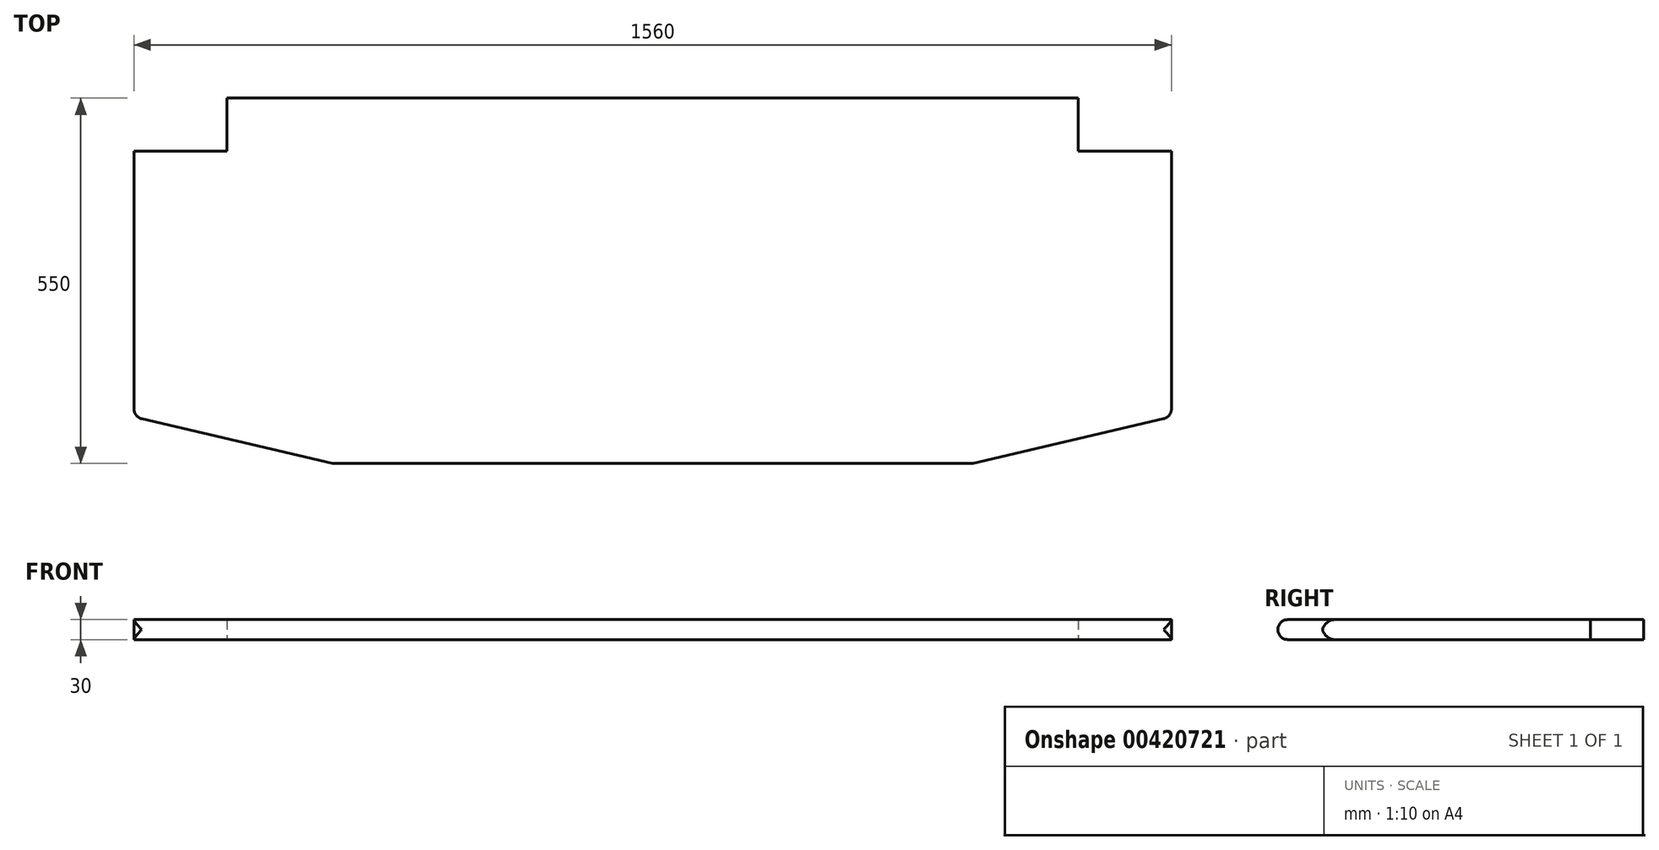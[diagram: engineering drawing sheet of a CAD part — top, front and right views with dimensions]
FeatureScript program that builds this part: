
annotation { "Feature Type Name" : "Feature", "Feature Type Description" : "" }
export const myFeature = defineFeature(function(context is Context, id is Id, definition is map)
    precondition{}
    {
        {
            var Q0;
            Q0=qCreatedBy(makeId("Top.planeOp"),FACE);
            cPlane(context, id + "F0", {"entities" : qUnion([Q0]), "cplaneType" : CPlaneType.OFFSET, "offset" : 750 * mm, "width" : 150 * mm, "height" : 150 * mm});
        }
        {
            var Q0;
            Q0=qCreatedBy(id+"F0.planeOp",FACE);
            var sketch = newSketch(context, id + "F1", { "sketchPlane" : qUnion([Q0])});
            skLineSegment(sketch, "E0", {"start": v(-640, 0) * mm, "end": v(640, 0) * mm});
            skLineSegment(sketch, "E1", {"start": v(780, -80) * mm, "end": v(780, -480) * mm});
            skLineSegment(sketch, "E2", {"start": v(780, -480) * mm, "end": v(480, -550) * mm});
            skLineSegment(sketch, "E3", {"start": v(480, -550) * mm, "end": v(-480, -550) * mm});
            skLineSegment(sketch, "E4", {"start": v(-480, -550) * mm, "end": v(-780, -480) * mm});
            skLineSegment(sketch, "E5", {"start": v(-780, -480) * mm, "end": v(-780, -80) * mm});
            skLineSegment(sketch, "E6", {"start": v(-780, -80) * mm, "end": v(-640, -80) * mm});
            skLineSegment(sketch, "E7", {"start": v(-640, -80) * mm, "end": v(-640, 0) * mm});
            skLineSegment(sketch, "E8", {"start": v(780, -80) * mm, "end": v(640, -80) * mm});
            skLineSegment(sketch, "E9", {"start": v(640, -80) * mm, "end": v(640, 0) * mm});
            skPoint(sketch, "E10.orphan", {"position": v(-780, 0) * mm});
            skPoint(sketch, "E11.orphan", {"position": v(780, 0) * mm});
            skSolve(sketch);
        }
        {
            var Q0;
            Q0 = qSketchRegion(id + "F1", true);
            extrude(context, id + "F2", {"entities" : qUnion([Q0]), "depth" : 30 * mm});
        }
        {
            var Q0;
            Q0=makeQuery(id+"F2.opExtrude","CAP_EDGE",EDGE,{"disambiguationData":[OSD([sQuery(id+"F1.wireOp",EDGE,"E4")])],"isStart":false});
            var Q1;
            Q1=makeQuery(id+"F2.opExtrude","SWEPT_FACE",FACE,{"disambiguationData":[OSD([sQuery(id+"F1.wireOp",EDGE,"E4")])]});
            var Q2;
            Q2=makeQuery(id+"F2.opExtrude","SWEPT_FACE",FACE,{"disambiguationData":[OSD([sQuery(id+"F1.wireOp",EDGE,"E3")])]});
            var Q3;
            Q3=makeQuery(id+"F2.opExtrude","SWEPT_FACE",FACE,{"disambiguationData":[OSD([sQuery(id+"F1.wireOp",EDGE,"E2")])]});
            var Q4;
            Q4=makeQuery(id+"F2.opExtrude","SWEPT_EDGE",EDGE,{"disambiguationData":[OSD([sQuery(id+"F1.wireOp",EDGE,"E3"),sQuery(id+"F1.wireOp",EDGE,"E4")])]});
            fillet(context, id + "F3", {"entities" : qUnion([Q0, Q1, Q2, Q3, Q4]), "radius" : 15 * mm, "tangentPropagation" : true, "allowEdgeOverflow" : false});
        }
    });
